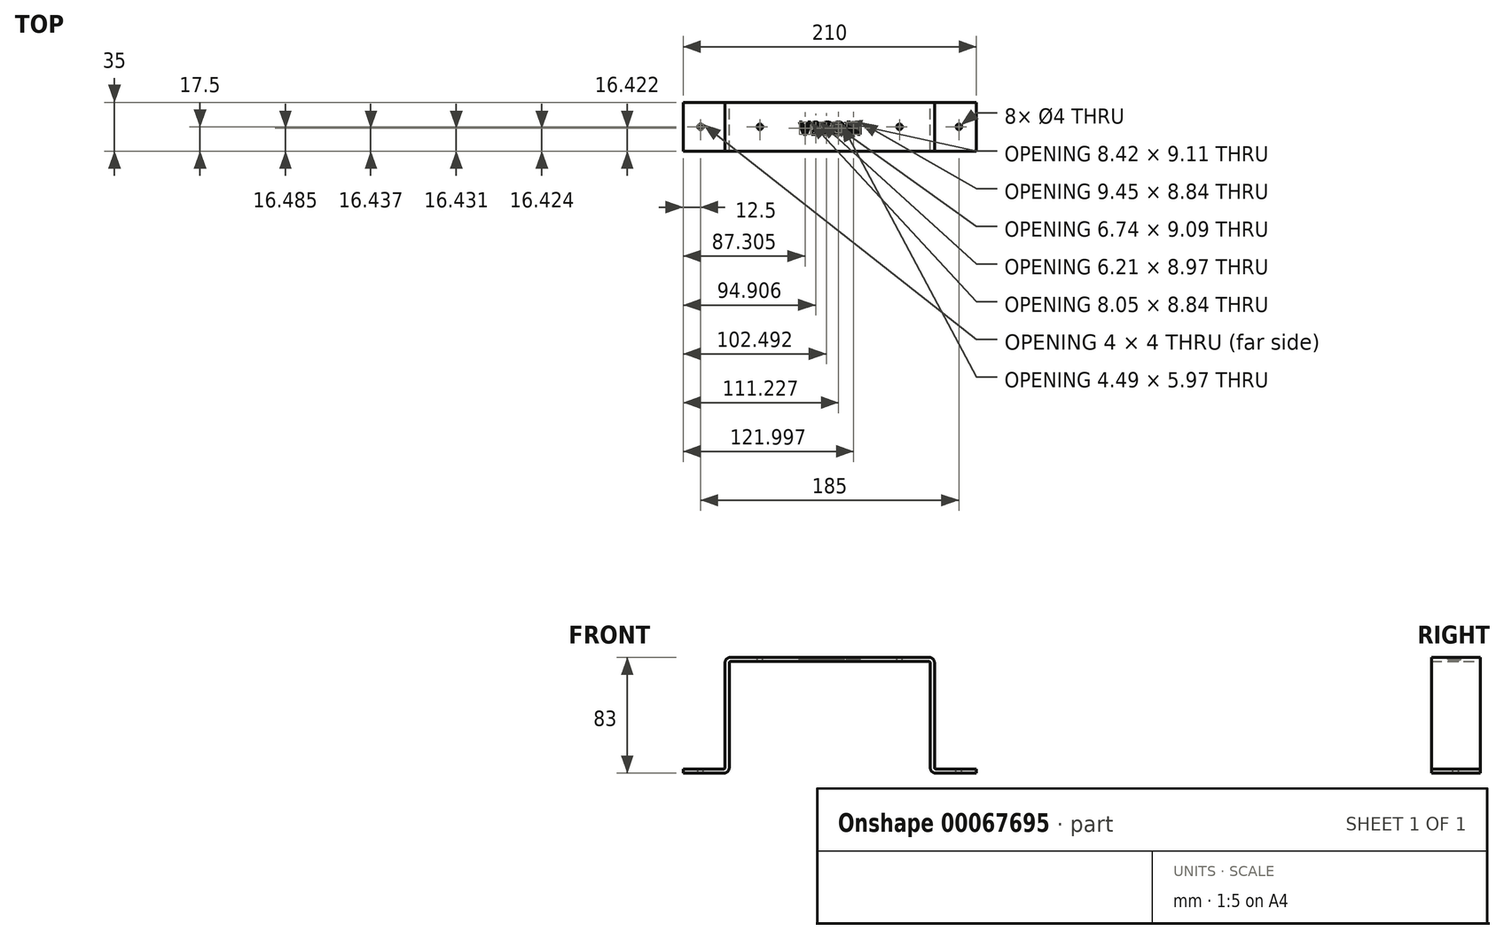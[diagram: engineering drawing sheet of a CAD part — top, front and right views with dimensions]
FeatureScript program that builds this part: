
annotation { "Feature Type Name" : "Feature", "Feature Type Description" : "" }
export const myFeature = defineFeature(function(context is Context, id is Id, definition is map)
    precondition{}
    {
        {
            var Q0;
            Q0=qCreatedBy(makeId("Front.planeOp"),FACE);
            var sketch = newSketch(context, id + "F0", { "sketchPlane" : qUnion([Q0])});
            skLineSegment(sketch, "E0", {"start": v(0, 0) * mm, "end": v(71, 0) * mm});
            skLineSegment(sketch, "E1", {"start": v(75, -4) * mm, "end": v(75, -79) * mm});
            skLineSegment(sketch, "E2", {"start": v(76, -80) * mm, "end": v(105, -80) * mm});
            skLineSegment(sketch, "E3.0", {"start": v(76, -83) * mm, "end": v(105, -83) * mm});
            skLineSegment(sketch, "E3.1", {"start": v(72, -4) * mm, "end": v(72, -79) * mm});
            skLineSegment(sketch, "E3.2", {"start": v(0, -3) * mm, "end": v(71, -3) * mm});
            skLineSegment(sketch, "E4", {"start": v(105, -80) * mm, "end": v(105, -83) * mm});
            skLineSegment(sketch, "E5", {"start": v(0, 0) * mm, "end": v(0, -3) * mm});
            skPoint(sketch, "E6.visualSharp", {"position": v(72, -3) * mm});
            skPoint(sketch, "E7.visualSharp", {"position": v(75, 0) * mm});
            skPoint(sketch, "E8.visualSharp", {"position": v(75, -80) * mm});
            skPoint(sketch, "E9.visualSharp", {"position": v(72, -83) * mm});
            skArc(sketch, "E10.filletArc", {"start": v(72, -4) * mm, "mid": v(71.7, -3.3) * mm, "end": v(71, -3) * mm});
            skArc(sketch, "E11.filletArc", {"start": v(75, -4) * mm, "mid": v(73.83, -1.17) * mm, "end": v(71, 0) * mm});
            skArc(sketch, "E12.filletArc", {"start": v(75, -79) * mm, "mid": v(75.3, -79.7) * mm, "end": v(76, -80) * mm});
            skArc(sketch, "E13.filletArc", {"start": v(72, -79) * mm, "mid": v(73.17, -81.83) * mm, "end": v(76, -83) * mm});
            skArc(sketch, "E14.MirrorCS", {"start": v(-72, -4) * mm, "mid": v(-71.7, -3.3) * mm, "end": v(-71, -3) * mm});
            skArc(sketch, "E15.MirrorCS", {"start": v(-75, -79) * mm, "mid": v(-75.3, -79.7) * mm, "end": v(-76, -80) * mm});
            skLineSegment(sketch, "E16.MirrorCS", {"start": v(-105, -80) * mm, "end": v(-105, -83) * mm});
            skArc(sketch, "E17.MirrorCS", {"start": v(-75, -4) * mm, "mid": v(-73.83, -1.17) * mm, "end": v(-71, 0) * mm});
            skArc(sketch, "E18.MirrorCS", {"start": v(-72, -79) * mm, "mid": v(-73.17, -81.83) * mm, "end": v(-76, -83) * mm});
            skPoint(sketch, "E19.MirrorP", {"position": v(-75, 0) * mm});
            skPoint(sketch, "E20.MirrorP", {"position": v(-72, -3) * mm});
            skPoint(sketch, "E21.MirrorP", {"position": v(-72, -83) * mm});
            skPoint(sketch, "E22.MirrorP", {"position": v(-75, -80) * mm});
            skLineSegment(sketch, "E23.MirrorCS", {"start": v(-75, -4) * mm, "end": v(-75, -79) * mm});
            skLineSegment(sketch, "E24.MirrorCS", {"start": v(-76, -80) * mm, "end": v(-105, -80) * mm});
            skLineSegment(sketch, "E25.MirrorCS", {"start": v(0, 0) * mm, "end": v(-71, 0) * mm});
            skLineSegment(sketch, "E26.MirrorCS", {"start": v(-76, -83) * mm, "end": v(-105, -83) * mm});
            skLineSegment(sketch, "E27.MirrorCS", {"start": v(0, -3) * mm, "end": v(-71, -3) * mm});
            skLineSegment(sketch, "E28.MirrorCS", {"start": v(-72, -4) * mm, "end": v(-72, -79) * mm});
            skSolve(sketch);
        }
        {
            var Q0;
            Q0 = qSketchRegion(id + "F0", true);
            extrude(context, id + "F1", {"entities" : qUnion([Q0]), "depth" : 35 * mm});
        }
        {
            var Q0;
            Q0=qCreatedBy(makeId("Top.planeOp"),FACE);
            var sketch = newSketch(context, id + "F2", { "sketchPlane" : qUnion([Q0])});
            skCircle(sketch, "E29", {"center": v(-50, -17.5) * mm, "radius": 2 * mm});
            skCircle(sketch, "E30.MirrorC", {"center": v(50, -17.5) * mm, "radius": 2 * mm});
            skSolve(sketch);
        }
        {
            var Q0;
            Q0 = qSketchRegion(id + "F2", true);
            extrude(context, id + "F3", {"entities" : qUnion([Q0]), "operationType" : NewBodyOperationType.REMOVE, "oppositeDirection" : true, "depth" : 25 * mm});
        }
        {
            var Q0;
            Q0=makeQuery(id+"F1.opExtrude","SWEPT_FACE",FACE,{"disambiguationData":[OSD([sQuery(id+"F0.wireOp",EDGE,"E24.MirrorCS")])]});
            var sketch = newSketch(context, id + "F4", { "sketchPlane" : qUnion([Q0])});
            skCircle(sketch, "E31", {"center": v(-92.5, -17.5) * mm, "radius": 2 * mm});
            skCircle(sketch, "E32.MirrorC", {"center": v(92.5, -17.5) * mm, "radius": 2 * mm});
            skSolve(sketch);
        }
        {
            var Q0;
            Q0 = qSketchRegion(id + "F4", true);
            extrude(context, id + "F5", {"entities" : qUnion([Q0]), "operationType" : NewBodyOperationType.REMOVE, "oppositeDirection" : true, "depth" : 25 * mm});
        }
        {
            var Q0;
            Q0=makeQuery(id+"F1.opExtrude","SWEPT_FACE",FACE,{"disambiguationData":[OSD([sQuery(id+"F0.wireOp",EDGE,"E0"),sQuery(id+"F0.wireOp",EDGE,"E25.MirrorCS")])]});
            var sketch = newSketch(context, id + "F6", { "sketchPlane" : qUnion([Q0])});
            skText(sketch, "E33", { "text": "V2COM", "fontName": "OpenSans-Bold.ttf"});
            const initialGuessF6  = {"E33": [-0.02172, -0.023, 1, 0, 0.00892]};
            skSetInitialGuess(sketch, initialGuessF6);
            skSolve(sketch);
        }
        {
            var Q0;
            Q0 = qSketchRegion(id + "F6", true);
            extrude(context, id + "F7", {"entities" : qUnion([Q0]), "operationType" : NewBodyOperationType.REMOVE, "oppositeDirection" : true, "depth" : 1.5 * mm});
        }
    });
